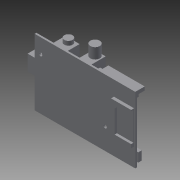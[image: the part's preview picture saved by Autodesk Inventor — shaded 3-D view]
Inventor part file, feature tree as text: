
AUTODESK INVENTOR PART (.ipt)
format: ipt  version: 2014 (Build 180170000, 170)  size: 246,272 bytes
history: native  units: mm
features: extrude x14, sketch x14
ambient origin geometry x8: Origin, YZ Plane, XZ Plane, XY Plane, X Axis, Y Axis, Z Axis, Center Point
bodies: Volumenkörper1 (feature_tree)
feature tree (28):
  extrude  "Extrusion1"  Depth=56.0mm
  extrude  "Extrusion2"  Depth=21.0mm
  extrude  "Extrusion3"  Depth=1.2mm
  extrude  "Extrusion4"  Depth=7.5mm
  extrude  "Extrusion5"  Depth=13.2mm
  extrude  "Extrusion6"  Depth=16.0mm TaperAngle=0.0deg
  extrude  "Extrusion7"  Depth=15.0mm
  extrude  "Extrusion8"  Depth=15.0mm
  extrude  "Extrusion9"  Depth=11.5mm
  extrude  "Extrusion10"  Depth=14.5mm
  extrude  "Extrusion11"  Depth=7.0mm
  extrude  "Extrusion12"  Depth=3.5mm TaperAngle=0.0deg
  extrude  "Extrusion13"  Depth=10.0mm
  extrude  "Extrusion14"  Depth=7.5mm
  sketch  "Skizze1"  dims[d0=85.0mm d1=56.0mm]
  sketch  "Skizze2"  dims[d2=1.5mm d3=0.0mm d4=21.0mm]
  sketch  "Skizze3"  dims[d5=16.0mm d6=1.2mm]
  sketch  "Skizze4"  dims[d7=13.4mm d8=0.0mm d9=7.5mm]
  sketch  "Skizze5"  dims[d10=17.4mm d11=13.2mm]
  sketch  "Skizze6"  dims[d12=6.6mm d13=16.0mm d14=0.0mm]
  sketch  "Skizze7"  dims[d15=1.0mm d16=15.0mm]
  sketch  "Skizze8"  dims[d17=11.8mm d18=15.0mm]
  sketch  "Skizze9"  dims[d19=5.5mm d20=0.0mm d21=11.5mm]
  sketch  "Skizze10"  dims[d22=12.0mm d23=14.5mm]
  sketch  "Skizze11"  dims[d24=10.0mm d25=0.0mm d26=7.0mm]
  sketch  "Skizze12"  dims[d27=3.5mm d28=3.5mm d29=0.0mm]
  sketch  "Skizze13"  dims[d30=10.0mm d31=10.0mm]
  sketch  "Skizze14"  dims[d32=2.5mm d33=7.5mm d34=14.5mm d35=0.0mm d36=8.0mm d37=0.0mm d38=9.0mm d39=0.0mm d40=32.7mm d41=5.0mm d42=1.0mm d43=1.0mm d44=2.5mm d45=0.0mm d50=1.0mm d51=1.0mm d52=1.0mm d53=1.0mm d54=6.0mm d55=0.0mm d56=1.0mm d57=7.5mm d58=5.6mm d59=4.0mm d60=3.0mm d61=0.0mm d62=15.5mm d63=17.0mm d64=28.0mm d65=1.0mm d66=0.5mm d67=0.0mm d69=24.0mm d70=3.0mm d71=3.0mm d72=45.0deg d73=19.0mm d74=2.0mm d75=0.0mm d76=2.9mm d77=25.5mm d78=18.0mm d79=2.9mm d80=5.0mm d81=12.5mm d82=2.0mm d83=0.0mm d84=1.0mm]
